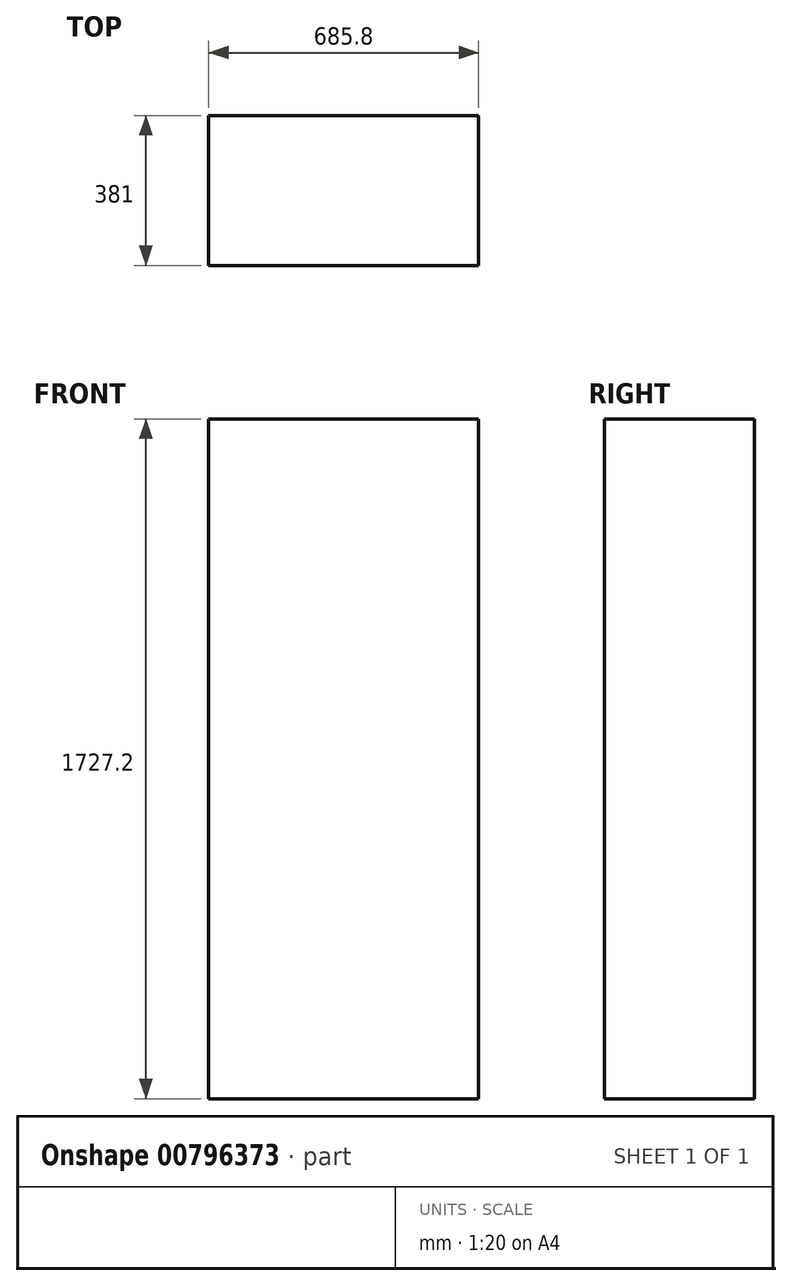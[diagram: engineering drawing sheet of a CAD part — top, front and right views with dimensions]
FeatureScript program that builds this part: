
annotation { "Feature Type Name" : "Feature", "Feature Type Description" : "" }
export const myFeature = defineFeature(function(context is Context, id is Id, definition is map)
    precondition{}
    {
        {
            var Q0;
            Q0=qCreatedBy(makeId("Top.planeOp"),FACE);
            var sketch = newSketch(context, id + "F0", { "sketchPlane" : qUnion([Q0])});
            skLineSegment(sketch, "E0.bottom", {"start": v(0, 0) * mm, "end": v(685.8, 0) * mm});
            skLineSegment(sketch, "E0.top", {"start": v(0, -381) * mm, "end": v(685.8, -381) * mm});
            skLineSegment(sketch, "E0.left", {"start": v(0, 0) * mm, "end": v(0, -381) * mm});
            skLineSegment(sketch, "E0.right", {"start": v(685.8, 0) * mm, "end": v(685.8, -381) * mm});
            skSolve(sketch);
        }
        {
            var Q0;
            Q0=makeQuery(id+"F0.imprint","IMPRINT",FACE,{"disambiguationData":[TD([[makeQuery(id+"F0.imprint","IMPRINT",EDGE,{"derivedFrom":sQuery(id+"F0.wireOp",EDGE,"E0.bottom")}),-1.0]])]});
            extrude(context, id + "F1", {"entities" : qUnion([Q0]), "depth" : 1727.2 * mm, "offsetDistance" : 25.4 * mm});
        }
    });
